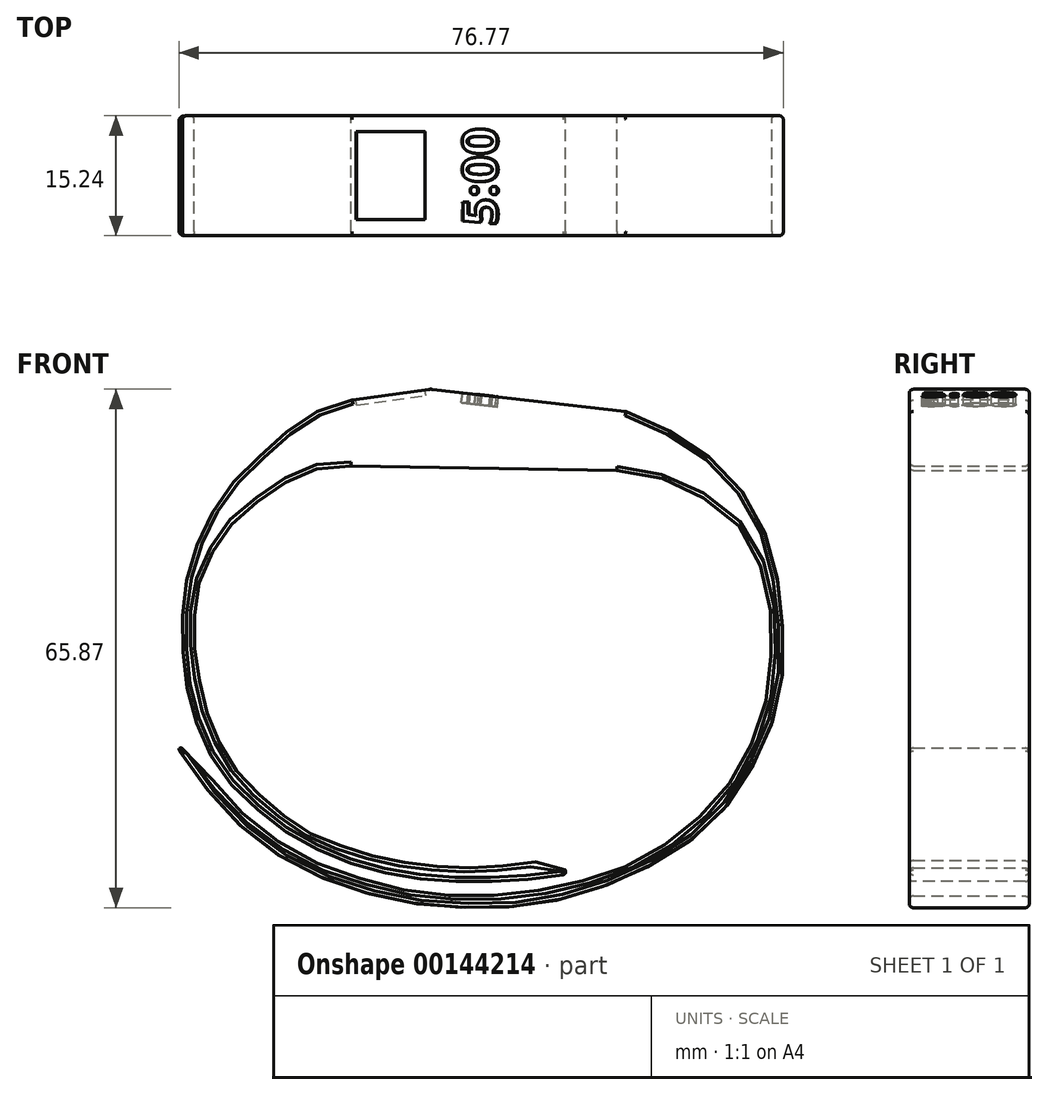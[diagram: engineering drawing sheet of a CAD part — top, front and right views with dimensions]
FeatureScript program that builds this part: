
annotation { "Feature Type Name" : "Feature", "Feature Type Description" : "" }
export const myFeature = defineFeature(function(context is Context, id is Id, definition is map)
    precondition{}
    {
        {
            var Q0;
            Q0=qCreatedBy(makeId("Right.planeOp"),FACE);
            var sketch = newSketch(context, id + "F0", { "sketchPlane" : qUnion([Q0])});
            skLineSegment(sketch, "E0.bottom", {"start": v(21.06, 43.42) * mm, "end": v(-21.06, 43.42) * mm});
            skLineSegment(sketch, "E0.top", {"start": v(21.06, 58.18) * mm, "end": v(-21.06, 58.18) * mm});
            skLineSegment(sketch, "E0.left", {"start": v(21.06, 43.42) * mm, "end": v(21.06, 58.18) * mm});
            skLineSegment(sketch, "E0.right", {"start": v(-21.06, 43.42) * mm, "end": v(-21.06, 58.18) * mm});
            skPoint(sketch, "E0.middle", {"position": v(0, 50.8) * mm});
            skLineSegment(sketch, "E1.bottom", {"start": v(21.06, -48.2) * mm, "end": v(-21.06, -48.2) * mm});
            skLineSegment(sketch, "E1.top", {"start": v(21.06, -43.85) * mm, "end": v(-21.06, -43.85) * mm});
            skLineSegment(sketch, "E1.left", {"start": v(21.06, -48.2) * mm, "end": v(21.06, -43.85) * mm});
            skLineSegment(sketch, "E1.right", {"start": v(-21.06, -48.2) * mm, "end": v(-21.06, -43.85) * mm});
            skPoint(sketch, "E1.middle", {"position": v(0, -46.02) * mm});
            skSolve(sketch);
        }
        {
            var Q0;
            Q0=qCreatedBy(makeId("Front.planeOp"),FACE);
            var sketch = newSketch(context, id + "F1", { "sketchPlane" : qUnion([Q0])});
            skFitSpline(sketch, "E2", {"points": [v(21.38, 29.41) * mm, v(23.41, 28.7) * mm, v(25.89, 27.49) * mm, v(28.83, 25.85) * mm, v(31.72, 23.83) * mm, v(34.34, 21.38) * mm, v(37.28, 17.67) * mm, v(38.97, 14.18) * mm, v(40.17, 10.26) * mm, v(40.94, 6.22) * mm, v(41.32, 1.8) * mm, v(41.38, -2.66) * mm, v(40.83, -6.97) * mm, v(39.3, -11.94) * mm, v(36.8, -16.9) * mm, v(33.63, -21.37) * mm, v(30.2, -24.64) * mm, v(26.16, -27.31) * mm, v(21.42, -29.77) * mm, v(17.38, -31.3) * mm, v(12.42, -32.71) * mm, v(7.19, -33.47) * mm, v(2.66, -33.64) * mm, v(-2.37, -33.43) * mm, v(-8.08, -32.6) * mm, v(-13.91, -31.02) * mm, v(-18.93, -29.06) * mm, v(-22.9, -26.82) * mm, v(-25.96, -24.59) * mm, v(-28.47, -22.35) * mm, v(-31.09, -19.46) * mm, v(-33.32, -16.46) * mm, v(-34.74, -14.4) * mm, v(-35.34, -13.4) * mm, v(-34.14, -13.63) * mm, v(-33.1, -14.6) * mm, v(-31.41, -16.95) * mm, v(-29.45, -19.52) * mm, v(-27.3, -21.66) * mm, v(-24.74, -23.86) * mm, v(-22.3, -25.51) * mm, v(-18.1, -27.86) * mm, v(-13.53, -29.55) * mm, v(-7.7, -31.18) * mm, v(-2.52, -31.95) * mm, v(3.82, -32.13) * mm, v(7.13, -31.84) * mm, v(12.2, -31.13) * mm, v(17, -29.93) * mm, v(20.87, -28.62) * mm, v(25.34, -26.28) * mm, v(28.72, -23.88) * mm, v(33.25, -19.57) * mm, v(35.58, -16.25) * mm, v(37.26, -13.09) * mm, v(38.96, -8.46) * mm, v(39.56, -4.96) * mm, v(39.92, 0) * mm, v(39.66, 5.08) * mm, v(38.53, 9.81) * mm, v(36.27, 14.29) * mm, v(30.7, 18.77) * mm, v(26.33, 20.77) * mm, v(23.02, 21.6) * mm, v(20.3, 21.92) * mm], "startDerivative": vector(227.85, -32.22) * mm, "endDerivative": vector(-220.58, -1.9) * mm});
            skLineSegment(sketch, "E3", {"start": v(21.38, 29.41) * mm, "end": v(20.3, 21.92) * mm});
            skFitSpline(sketch, "E4", {"points": [v(-13.33, 30.88) * mm, v(-16.03, 30.1) * mm, v(-18.1, 29.2) * mm, v(-20.03, 27.98) * mm, v(-22.54, 26.08) * mm, v(-24.57, 24.22) * mm, v(-26.73, 22.18) * mm, v(-28.9, 19.9) * mm, v(-31.02, 16.73) * mm, v(-32.36, 14.22) * mm, v(-33.27, 11.8) * mm, v(-34.18, 8.85) * mm, v(-34.78, 5.26) * mm, v(-34.91, 1.54) * mm, v(-34.83, -1.92) * mm, v(-34.44, -5.3) * mm, v(-33.74, -8.24) * mm, v(-32.92, -10.7) * mm, v(-31.8, -13.35) * mm, v(-30.24, -16.03) * mm, v(-28.12, -18.63) * mm, v(-25.95, -20.66) * mm, v(-23.7, -22.52) * mm, v(-21.06, -24.43) * mm, v(-17.82, -26.16) * mm, v(-13.8, -27.89) * mm, v(-9.55, -29.1) * mm, v(-5.57, -29.84) * mm, v(-1.42, -30.23) * mm, v(2.13, -30.31) * mm, v(6.63, -30.18) * mm, v(10.44, -29.92) * mm, v(13.73, -29.23) * mm, v(12.9, -28.02) * mm, v(11, -27.67) * mm, v(8.36, -28.06) * mm, v(5.2, -28.36) * mm, v(2, -28.58) * mm, v(-2.11, -28.45) * mm, v(-5.88, -28.02) * mm, v(-8.82, -27.54) * mm, v(-12.02, -26.68) * mm, v(-15.96, -25.38) * mm, v(-18.77, -24.12) * mm, v(-21.58, -22.26) * mm, v(-25.05, -19.4) * mm, v(-27.38, -17.07) * mm, v(-29.46, -14.17) * mm, v(-31.67, -9.24) * mm, v(-32.36, -6.73) * mm, v(-33.1, -3) * mm, v(-33.4, 0) * mm, v(-33.35, 3.75) * mm, v(-32.97, 7.12) * mm, v(-31.45, 10.8) * mm, v(-29.76, 13.83) * mm, v(-26.47, 17.12) * mm, v(-23.46, 19.32) * mm, v(-21.05, 20.83) * mm, v(-18.19, 22.03) * mm, v(-13.52, 22.47) * mm], "startDerivative": vector(-142.9, -45.93) * mm, "endDerivative": vector(248.38, -17.33) * mm});
            skLineSegment(sketch, "E5", {"start": v(-13.33, 30.88) * mm, "end": v(-3.63, 32.2) * mm});
            skLineSegment(sketch, "E6", {"start": v(-13.33, 30.88) * mm, "end": v(-13.52, 22.47) * mm});
            skLineSegment(sketch, "E7", {"start": v(-3.38, 32.24) * mm, "end": v(-3.38, 22.3) * mm});
            skLineSegment(sketch, "E8", {"start": v(21.38, 29.41) * mm, "end": v(-3.13, 32.21) * mm});
            skPoint(sketch, "E9.visualSharp", {"position": v(-3.38, 32.24) * mm});
            skArc(sketch, "E9.filletArc", {"start": v(-3.13, 32.21) * mm, "mid": v(-3.38, 32.23) * mm, "end": v(-3.63, 32.2) * mm});
            skLineSegment(sketch, "E10", {"start": v(-13.52, 22.47) * mm, "end": v(-3.38, 22.3) * mm});
            skLineSegment(sketch, "E11", {"start": v(-3.38, 22.3) * mm, "end": v(20.3, 21.92) * mm});
            skSolve(sketch);
        }
        {
            var Q0;
            Q0=qSketchRegion(id+"F1",true);
            extrude(context, id + "F2", {"entities" : qUnion([Q0]), "endBound" : BoundingType.SYMMETRIC, "depth" : 15.24 * mm});
        }
        {
            var Q0;
            Q0=makeQuery(id+"F2.opExtrude","SWEPT_FACE",FACE,{"disambiguationData":[OSD([sQuery(id+"F1.wireOp",EDGE,"E5")])]});
            var sketch = newSketch(context, id + "F3", { "sketchPlane" : qUnion([Q0])});
            skLineSegment(sketch, "E12.bottom", {"start": v(-8.57, -5.59) * mm, "end": v(0.32, -5.59) * mm});
            skLineSegment(sketch, "E12.top", {"start": v(-8.57, 5.59) * mm, "end": v(0.32, 5.59) * mm});
            skLineSegment(sketch, "E12.left", {"start": v(-8.57, -5.59) * mm, "end": v(-8.57, 5.59) * mm});
            skLineSegment(sketch, "E12.right", {"start": v(0.32, -5.59) * mm, "end": v(0.32, 5.59) * mm});
            skSolve(sketch);
        }
        {
            var Q0;
            Q0=qSketchRegion(id+"F3",true);
            extrude(context, id + "F4", {"entities" : qUnion([Q0]), "operationType" : NewBodyOperationType.REMOVE, "oppositeDirection" : true, "depth" : 0.71 * mm});
        }
        {
            var Q0;
            Q0=makeQuery(id+"F2.opExtrude","SWEPT_FACE",FACE,{"disambiguationData":[OSD([sQuery(id+"F1.wireOp",EDGE,"E8")])]});
            var sketch = newSketch(context, id + "F5", { "sketchPlane" : qUnion([Q0])});
            skText(sketch, "E13", { "text": "5:00\n", "fontName": "OpenSans-Bold.ttf"});
            const initialGuessF5  = {"E13": [0.00156, -0.00635, 0, 1, 0.00451]};
            skSetInitialGuess(sketch, initialGuessF5);
            skSolve(sketch);
        }
        {
            var Q0;
            Q0=qSketchRegion(id+"F5",true);
            extrude(context, id + "F6", {"entities" : qUnion([Q0]), "operationType" : NewBodyOperationType.REMOVE, "oppositeDirection" : true, "depth" : 1.27 * mm});
        }
        {
            var Q0;
            Q0=makeQuery(id+"F2.opExtrude","CAP_EDGE",EDGE,{"disambiguationData":[OSD([sQuery(id+"F1.wireOp",EDGE,"E4")])],"isStart":false});
            var Q1;
            Q1=makeQuery(id+"F2.opExtrude","CAP_EDGE",EDGE,{"disambiguationData":[OSD([sQuery(id+"F1.wireOp",EDGE,"E10"),sQuery(id+"F1.wireOp",EDGE,"E11")])],"isStart":false});
            var Q2;
            Q2=makeQuery(id+"F2.opExtrude","CAP_EDGE",EDGE,{"disambiguationData":[OSD([sQuery(id+"F1.wireOp",EDGE,"E2")])],"isStart":false});
            var Q3;
            Q3=makeQuery(id+"F2.opExtrude","CAP_EDGE",EDGE,{"disambiguationData":[OSD([sQuery(id+"F1.wireOp",EDGE,"E10"),sQuery(id+"F1.wireOp",EDGE,"E11")])],"isStart":true});
            var Q4;
            Q4=makeQuery(id+"F2.opExtrude","CAP_EDGE",EDGE,{"disambiguationData":[OSD([sQuery(id+"F1.wireOp",EDGE,"E4")])],"isStart":true});
            var Q5;
            Q5=makeQuery(id+"F2.opExtrude","CAP_EDGE",EDGE,{"disambiguationData":[OSD([sQuery(id+"F1.wireOp",EDGE,"E2")])],"isStart":true});
            fillet(context, id + "F7", {"entities" : qUnion([Q0, Q1, Q2, Q3, Q4, Q5]), "radius" : 0.5 * mm, "tangentPropagation" : true, "allowEdgeOverflow" : false});
        }
        {
            var Q0;
            Q0=makeQuery(id+"F2.opExtrude","CAP_EDGE",EDGE,{"disambiguationData":[OSD([sQuery(id+"F1.wireOp",EDGE,"E8")])],"isStart":false});
            var Q1;
            Q1=makeQuery(id+"F2.opExtrude","CAP_EDGE",EDGE,{"disambiguationData":[OSD([sQuery(id+"F1.wireOp",EDGE,"E8")])],"isStart":true});
            fillet(context, id + "F8", {"entities" : qUnion([Q0, Q1]), "radius" : 0.5 * mm, "tangentPropagation" : true, "allowEdgeOverflow" : false});
        }
    });
